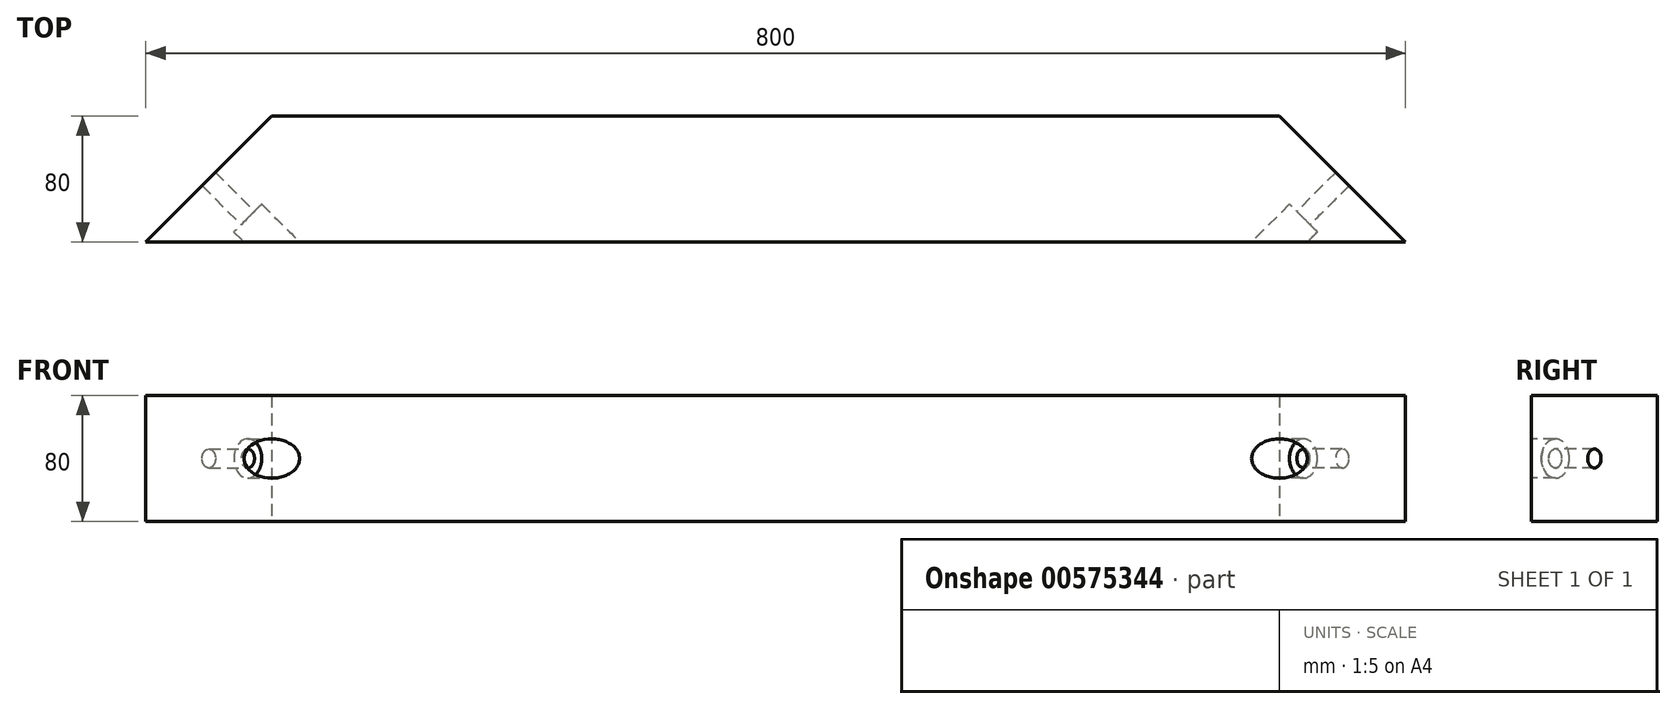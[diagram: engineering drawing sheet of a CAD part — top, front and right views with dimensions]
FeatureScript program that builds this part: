
annotation { "Feature Type Name" : "Feature", "Feature Type Description" : "" }
export const myFeature = defineFeature(function(context is Context, id is Id, definition is map)
    precondition{}
    {
        {
            var Q0;
            Q0=qCreatedBy(makeId("Top.planeOp"),FACE);
            var sketch = newSketch(context, id + "F0", { "sketchPlane" : qUnion([Q0])});
            skLineSegment(sketch, "E0.bottom", {"start": v(-320, 40) * mm, "end": v(320, 40) * mm});
            skLineSegment(sketch, "E0.top", {"start": v(-400, -40) * mm, "end": v(400, -40) * mm});
            skPoint(sketch, "E0.middle", {"position": v(0, 0) * mm});
            skLineSegment(sketch, "E1", {"start": v(-400, -40) * mm, "end": v(-320, 40) * mm});
            skLineSegment(sketch, "E2", {"start": v(400, -40) * mm, "end": v(320, 40) * mm});
            skSolve(sketch);
        }
        {
            var Q0;
            Q0=makeQuery(id+"F0.imprint","IMPRINT",FACE,{"disambiguationData":[TD([[makeQuery(id+"F0.imprint","IMPRINT",EDGE,{"derivedFrom":sQuery(id+"F0.wireOp",EDGE,"E0.bottom")}),-1.0]])]});
            extrude(context, id + "F1", {"entities" : qUnion([Q0]), "depth" : 80 * mm});
        }
        {
            var Q0;
            Q0=makeQuery(id+"F1.opExtrude","SWEPT_FACE",FACE,{"disambiguationData":[OSD([sQuery(id+"F0.wireOp",EDGE,"E1")])]});
            var sketch = newSketch(context, id + "F2", { "sketchPlane" : qUnion([Q0])});
            skLineSegment(sketch, "E3", {"start": v(197.99, 40) * mm, "end": v(311.13, 40) * mm, "construction": true});
            skLineSegment(sketch, "E4", {"start": v(254.56, 80) * mm, "end": v(254.56, 0) * mm, "construction": true});
            skPoint(sketch, "E5", {"position": v(254.56, 40) * mm});
            skSolve(sketch);
        }
        {
            var Q0;
            {var subQ0=sQuery(id+"F0.wireOp",EDGE,"E1");Q0=makeQuery(id+"F2.imprint","IMPRINT",FACE,{"disambiguationData":[TD([[makeQuery(id+"F2.imprint","IMPRINT",EDGE,{"derivedFrom":makeQuery(id+"F1.opExtrude","CAP_EDGE",EDGE,{"disambiguationData":[OSD([subQ0])],"isStart":true})}),-1.0]])]});}
            cPlane(context, id + "F3", {"entities" : qUnion([Q0]), "cplaneType" : CPlaneType.OFFSET, "offset" : 75 * mm, "oppositeDirection" : true, "width" : 150 * mm, "height" : 150 * mm});
        }
        {
            var Q0;
            Q0=qCreatedBy(id+"F3.planeOp",FACE);
            var sketch = newSketch(context, id + "F4", { "sketchPlane" : qUnion([Q0])});
            skLineSegment(sketch, "E6", {"start": v(197.99, 40) * mm, "end": v(311.13, 40) * mm, "construction": true});
            skLineSegment(sketch, "E7", {"start": v(254.56, 80) * mm, "end": v(254.56, 0) * mm, "construction": true});
            skPoint(sketch, "E8", {"position": v(254.56, 40) * mm});
            skSolve(sketch);
        }
        {
            var Q0;
            Q0=sQuery(id+"F4.wireOp",VERTEX,"E8");
            var Q1;
            Q1=makeQuery(id+"F1.opExtrude","SWEPT_BODY",BODY,{"disambiguationData":[OSD([sQuery(id+"F0.wireOp",EDGE,"E0.bottom"),sQuery(id+"F0.wireOp",EDGE,"E0.top"),sQuery(id+"F0.wireOp",EDGE,"E1"),sQuery(id+"F0.wireOp",EDGE,"E2")])]});
            hole(context, id + "F5", {"style" : HoleStyle.C_BORE, "endStyle" : HoleEndStyle.THROUGH, "oppositeDirection" : true, "holeDiameter" : 12 * mm, "cBoreDiameter" : 25 * mm, "cBoreDepth" : 40 * mm, "startFromSketch" : true, "locations" : qUnion([Q0]), "scope" : qUnion([Q1]), "isTappedThrough" : true});
        }
        {
            var Q0;
            Q0=makeQuery(id+"F1.opExtrude","SWEPT_FACE",FACE,{"disambiguationData":[OSD([sQuery(id+"F0.wireOp",EDGE,"E2")])]});
            cPlane(context, id + "F6", {"entities" : qUnion([Q0]), "cplaneType" : CPlaneType.OFFSET, "offset" : 75 * mm, "oppositeDirection" : true, "width" : 150 * mm, "height" : 150 * mm});
        }
        {
            var Q0;
            Q0=makeQuery(id+"F1.opExtrude","SWEPT_FACE",FACE,{"disambiguationData":[OSD([sQuery(id+"F0.wireOp",EDGE,"E2")])]});
            var sketch = newSketch(context, id + "F7", { "sketchPlane" : qUnion([Q0])});
            skLineSegment(sketch, "E9", {"start": v(-311.13, 40) * mm, "end": v(-197.99, 40) * mm, "construction": true});
            skPoint(sketch, "E10", {"position": v(-254.56, 40) * mm});
            skSolve(sketch);
        }
        {
            var Q0;
            Q0=qCreatedBy(id+"F6.planeOp",FACE);
            var sketch = newSketch(context, id + "F8", { "sketchPlane" : qUnion([Q0])});
            skLineSegment(sketch, "E11", {"start": v(-311.13, 40) * mm, "end": v(-197.99, 40) * mm, "construction": true});
            skLineSegment(sketch, "E12", {"start": v(-395.98, 80) * mm, "end": v(-395.98, 0) * mm, "construction": true});
            skPoint(sketch, "E13", {"position": v(-254.56, 40) * mm});
            skSolve(sketch);
        }
        {
            var Q0;
            Q0=sQuery(id+"F8.wireOp",VERTEX,"E13");
            var Q1;
            Q1=makeQuery(id+"F1.opExtrude","SWEPT_BODY",BODY,{"disambiguationData":[OSD([sQuery(id+"F0.wireOp",EDGE,"E0.bottom"),sQuery(id+"F0.wireOp",EDGE,"E0.top"),sQuery(id+"F0.wireOp",EDGE,"E1"),sQuery(id+"F0.wireOp",EDGE,"E2")])]});
            hole(context, id + "F9", {"style" : HoleStyle.C_BORE, "endStyle" : HoleEndStyle.THROUGH, "oppositeDirection" : true, "holeDiameter" : 12 * mm, "cBoreDiameter" : 25 * mm, "cBoreDepth" : 40 * mm, "startFromSketch" : true, "locations" : qUnion([Q0]), "scope" : qUnion([Q1]), "isTappedThrough" : true});
        }
    });
